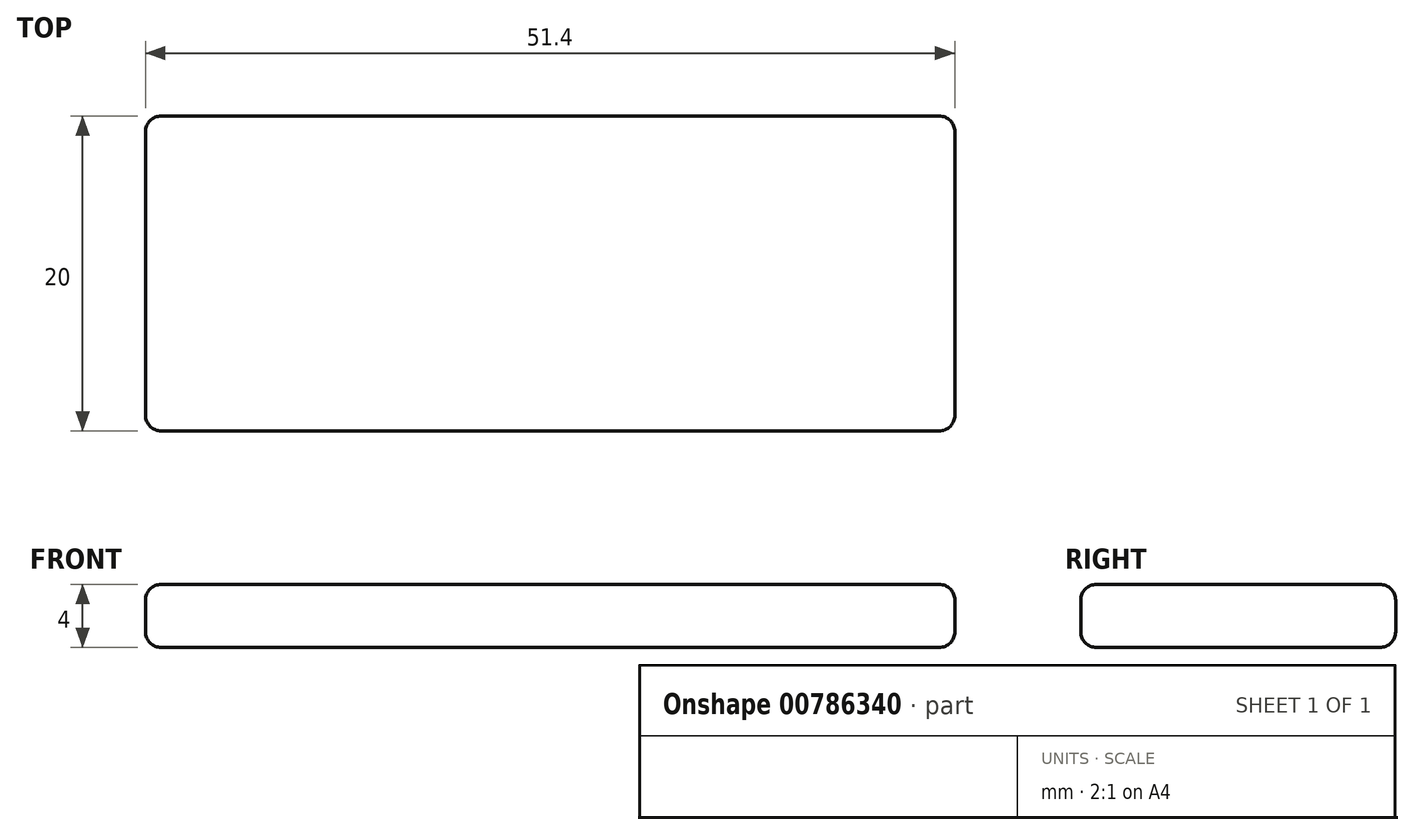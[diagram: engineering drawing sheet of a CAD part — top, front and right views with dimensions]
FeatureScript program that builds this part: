
annotation { "Feature Type Name" : "Feature", "Feature Type Description" : "" }
export const myFeature = defineFeature(function(context is Context, id is Id, definition is map)
    precondition{}
    {
        {
            var Q0;
            Q0=qCreatedBy(makeId("Front.planeOp"),FACE);
            var sketch = newSketch(context, id + "F0", { "sketchPlane" : qUnion([Q0])});
            skLineSegment(sketch, "E0.bottom", {"start": v(0, 0) * mm, "end": v(51.4, 0) * mm});
            skLineSegment(sketch, "E0.top", {"start": v(0, 4) * mm, "end": v(51.4, 4) * mm});
            skLineSegment(sketch, "E0.left", {"start": v(0, 0) * mm, "end": v(0, 4) * mm});
            skLineSegment(sketch, "E0.right", {"start": v(51.4, 0) * mm, "end": v(51.4, 4) * mm});
            skSolve(sketch);
        }
        {
            var Q0;
            Q0 = qSketchRegion(id + "F0", true);
            extrude(context, id + "F1", {"entities" : qUnion([Q0]), "depth" : 20 * mm, "offsetDistance" : 25 * mm});
        }
        {
            var Q0;
            Q0=makeQuery(id+"F1.opExtrude","CAP_FACE",FACE,{"disambiguationData":[OSD([sQuery(id+"F0.wireOp",EDGE,"E0.bottom"),sQuery(id+"F0.wireOp",EDGE,"E0.top"),sQuery(id+"F0.wireOp",EDGE,"E0.left"),sQuery(id+"F0.wireOp",EDGE,"E0.right")])],"isStart":false});
            var Q1;
            Q1=makeQuery(id+"F1.opExtrude","SWEPT_FACE",FACE,{"disambiguationData":[OSD([sQuery(id+"F0.wireOp",EDGE,"E0.right")])]});
            var Q2;
            Q2=makeQuery(id+"F1.opExtrude","CAP_FACE",FACE,{"disambiguationData":[OSD([sQuery(id+"F0.wireOp",EDGE,"E0.bottom"),sQuery(id+"F0.wireOp",EDGE,"E0.top"),sQuery(id+"F0.wireOp",EDGE,"E0.left"),sQuery(id+"F0.wireOp",EDGE,"E0.right")])],"isStart":true});
            var Q3;
            Q3=makeQuery(id+"F1.opExtrude","SWEPT_FACE",FACE,{"disambiguationData":[OSD([sQuery(id+"F0.wireOp",EDGE,"E0.left")])]});
            fillet(context, id + "F2", {"entities" : qUnion([Q0, Q1, Q2, Q3]), "radius" : 1 * mm, "tangentPropagation" : true, "allowEdgeOverflow" : false});
        }
    });
